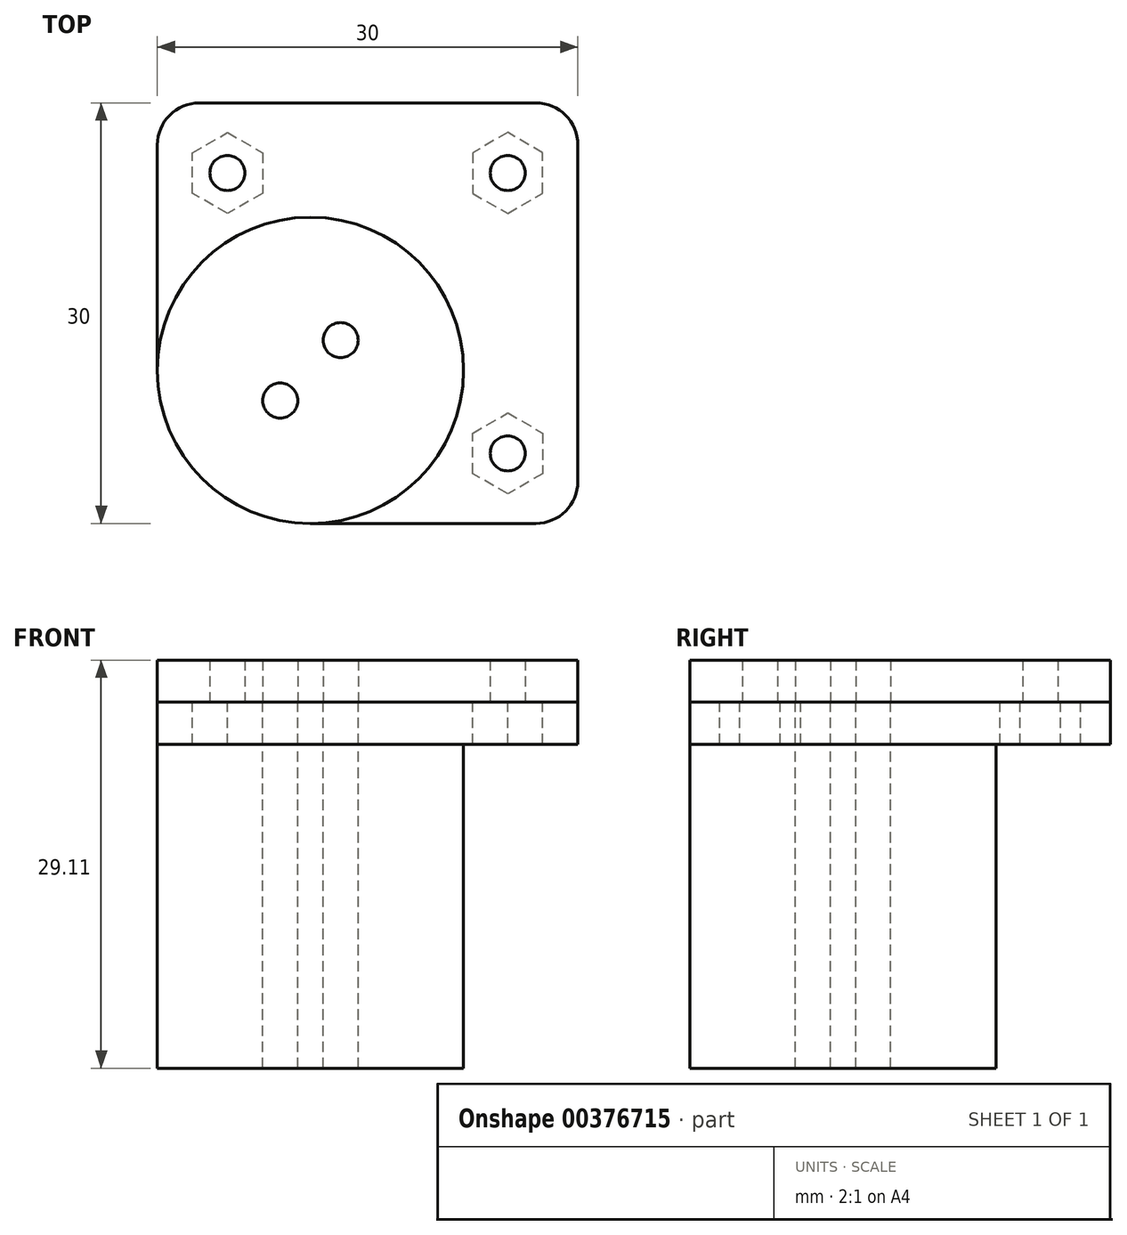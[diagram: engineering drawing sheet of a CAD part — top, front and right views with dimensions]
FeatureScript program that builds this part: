
annotation { "Feature Type Name" : "Feature", "Feature Type Description" : "" }
export const myFeature = defineFeature(function(context is Context, id is Id, definition is map)
    precondition{}
    {
        {
            var Q0;
            Q0=qCreatedBy(makeId("Top.planeOp"),FACE);
            var sketch = newSketch(context, id + "F0", { "sketchPlane" : qUnion([Q0])});
            skCircle(sketch, "E0", {"center": v(0, 0) * mm, "radius": 10.92 * mm});
            skSolve(sketch);
        }
        {
            var Q0;
            Q0 = qSketchRegion(id + "F0", true);
            extrude(context, id + "F1", {"entities" : qUnion([Q0]), "depth" : 23.1 * mm});
        }
        {
            var Q0;
            Q0=makeQuery(id+"F1.opExtrude","CAP_FACE",FACE,{"disambiguationData":[OSD([sQuery(id+"F0.wireOp",EDGE,"E0")])],"isStart":false});
            var sketch = newSketch(context, id + "F2", { "sketchPlane" : qUnion([Q0])});
            skArc(sketch, "E1", {"start": v(-10.92, 0) * mm, "mid": v(-7.72, -7.72) * mm, "end": v(0, -10.92) * mm});
            skLineSegment(sketch, "E2", {"start": v(0, 0) * mm, "end": v(0, -10.92) * mm, "construction": true});
            skLineSegment(sketch, "E3", {"start": v(0, 0) * mm, "end": v(-10.92, 0) * mm, "construction": true});
            skLineSegment(sketch, "E4", {"start": v(0, -10.92) * mm, "end": v(19.08, -10.92) * mm});
            skLineSegment(sketch, "E5", {"start": v(19.08, -10.92) * mm, "end": v(19.08, 19.08) * mm});
            skLineSegment(sketch, "E6", {"start": v(19.08, 19.08) * mm, "end": v(-10.92, 19.08) * mm});
            skLineSegment(sketch, "E7", {"start": v(-10.92, 19.08) * mm, "end": v(-10.92, 0) * mm});
            skSolve(sketch);
        }
        {
            var Q0;
            Q0 = qSketchRegion(id + "F2", true);
            extrude(context, id + "F3", {"entities" : qUnion([Q0]), "depth" : 3 * mm});
        }
        {
            var Q0;
            Q0=makeQuery(id+"F3.opExtrude","SWEPT_EDGE",EDGE,{"disambiguationData":[OSD([sQuery(id+"F2.wireOp",EDGE,"E4"),sQuery(id+"F2.wireOp",EDGE,"E5")])]});
            var Q1;
            Q1=makeQuery(id+"F3.opExtrude","SWEPT_EDGE",EDGE,{"disambiguationData":[OSD([sQuery(id+"F2.wireOp",EDGE,"E5"),sQuery(id+"F2.wireOp",EDGE,"E6")])]});
            var Q2;
            Q2=makeQuery(id+"F3.opExtrude","SWEPT_EDGE",EDGE,{"disambiguationData":[OSD([sQuery(id+"F2.wireOp",EDGE,"E6"),sQuery(id+"F2.wireOp",EDGE,"E7")])]});
            fillet(context, id + "F4", {"entities" : qUnion([Q0, Q1, Q2]), "radius" : 3 * mm, "tangentPropagation" : true, "allowEdgeOverflow" : false});
        }
        {
            var Q0;
            Q0=makeQuery(id+"F3.opExtrude","CAP_FACE",FACE,{"disambiguationData":[OSD([sQuery(id+"F2.wireOp",EDGE,"E1"),sQuery(id+"F2.wireOp",EDGE,"E4"),sQuery(id+"F2.wireOp",EDGE,"E5"),sQuery(id+"F2.wireOp",EDGE,"E6"),sQuery(id+"F2.wireOp",EDGE,"E7")])],"isStart":false});
            var sketch = newSketch(context, id + "F5", { "sketchPlane" : qUnion([Q0])});
            skLineSegment(sketch, "E8", {"start": v(-10.92, 0) * mm, "end": v(19.08, 0) * mm, "construction": true});
            skLineSegment(sketch, "E9", {"start": v(0, -10.92) * mm, "end": v(0, 19.08) * mm, "construction": true});
            skLineSegment(sketch, "E10", {"start": v(-7.72, -7.72) * mm, "end": v(0, 0) * mm, "construction": true});
            skLineSegment(sketch, "E11", {"start": v(-10.92, 10.92) * mm, "end": v(10.92, -10.92) * mm, "construction": true});
            skPoint(sketch, "E12", {"position": v(-2.16, -2.16) * mm});
            skPoint(sketch, "E13.MirrorP", {"position": v(2.16, 2.16) * mm});
            skSolve(sketch);
        }
        {
            var Q0;
            Q0=sQuery(id+"F5.wireOp",VERTEX,"E12");
            var Q1;
            Q1=sQuery(id+"F5.wireOp",VERTEX,"E13.MirrorP");
            var Q2;
            Q2=makeQuery(id+"F3.opExtrude","SWEPT_BODY",BODY,{"disambiguationData":[OSD([sQuery(id+"F2.wireOp",EDGE,"E1"),sQuery(id+"F2.wireOp",EDGE,"E4"),sQuery(id+"F2.wireOp",EDGE,"E5"),sQuery(id+"F2.wireOp",EDGE,"E6"),sQuery(id+"F2.wireOp",EDGE,"E7")])]});
            var Q3;
            Q3=makeQuery(id+"F1.opExtrude","SWEPT_BODY",BODY,{"disambiguationData":[OSD([sQuery(id+"F0.wireOp",EDGE,"E0")])]});
            hole(context, id + "F6", {"style" : HoleStyle.SIMPLE, "endStyle" : HoleEndStyle.THROUGH, "holeDiameter" : 2.5 * mm, "isTappedThrough" : true, "tappedDepth" : 12 * mm, "tapClearance" : 3, "locations" : qUnion([Q0, Q1]), "scope" : qUnion([Q2, Q3])});
        }
        {
            var Q0;
            Q0=makeQuery(id+"F3.opExtrude","CAP_FACE",FACE,{"disambiguationData":[OSD([sQuery(id+"F2.wireOp",EDGE,"E1"),sQuery(id+"F2.wireOp",EDGE,"E4"),sQuery(id+"F2.wireOp",EDGE,"E5"),sQuery(id+"F2.wireOp",EDGE,"E6"),sQuery(id+"F2.wireOp",EDGE,"E7")])],"isStart":false});
            extrude(context, id + "F7", {"entities" : qUnion([Q0]), "depth" : 3 * mm});
        }
        {
            var Q0;
            Q0=makeQuery(id+"F3.opExtrude","CAP_FACE",FACE,{"disambiguationData":[OSD([sQuery(id+"F2.wireOp",EDGE,"E1"),sQuery(id+"F2.wireOp",EDGE,"E4"),sQuery(id+"F2.wireOp",EDGE,"E5"),sQuery(id+"F2.wireOp",EDGE,"E6"),sQuery(id+"F2.wireOp",EDGE,"E7")])],"isStart":false});
            var sketch = newSketch(context, id + "F8", { "sketchPlane" : qUnion([Q0])});
            skLineSegment(sketch, "E14", {"start": v(19.08, 4.08) * mm, "end": v(-10.92, 4.08) * mm, "construction": true});
            skLineSegment(sketch, "E15", {"start": v(4.08, 19.08) * mm, "end": v(4.08, -10.92) * mm, "construction": true});
            skPoint(sketch, "E15.endSnap0", {"position": v(4.08, 4.08) * mm});
            skPoint(sketch, "E16", {"position": v(-5.92, 14.08) * mm});
            skPoint(sketch, "E17.MirrorP", {"position": v(14.08, 14.08) * mm});
            skPoint(sketch, "E18.MirrorP", {"position": v(14.08, -5.92) * mm});
            skCircle(sketch, "E19.cCircle", {"center": v(-5.92, 14.08) * mm, "radius": 2.5 * mm, "construction": true});
            skLineSegment(sketch, "E19.0", {"start": v(-3.42, 15.52) * mm, "end": v(-3.42, 12.63) * mm});
            skLineSegment(sketch, "E19.1", {"start": v(-3.42, 12.63) * mm, "end": v(-5.92, 11.2) * mm});
            skLineSegment(sketch, "E19.2", {"start": v(-5.92, 11.2) * mm, "end": v(-8.42, 12.63) * mm});
            skLineSegment(sketch, "E19.3", {"start": v(-8.42, 12.63) * mm, "end": v(-8.42, 15.52) * mm});
            skLineSegment(sketch, "E19.4", {"start": v(-8.42, 15.52) * mm, "end": v(-5.92, 16.96) * mm});
            skLineSegment(sketch, "E19.5", {"start": v(-5.92, 16.96) * mm, "end": v(-3.42, 15.52) * mm});
            skPoint(sketch, "E19.0.midPoint", {"position": v(-3.42, 14.08) * mm});
            skLineSegment(sketch, "E20.MirrorCS", {"start": v(11.58, 15.52) * mm, "end": v(11.58, 12.63) * mm});
            skLineSegment(sketch, "E21.MirrorCS", {"start": v(16.58, 15.52) * mm, "end": v(14.08, 16.96) * mm});
            skLineSegment(sketch, "E22.MirrorCS", {"start": v(11.58, 12.63) * mm, "end": v(14.08, 11.2) * mm});
            skLineSegment(sketch, "E23.MirrorCS", {"start": v(16.58, 12.63) * mm, "end": v(16.58, 15.52) * mm});
            skLineSegment(sketch, "E24.MirrorCS", {"start": v(14.08, 16.96) * mm, "end": v(11.58, 15.52) * mm});
            skCircle(sketch, "E25.MirrorC", {"center": v(14.08, 14.08) * mm, "radius": 2.5 * mm, "construction": true});
            skLineSegment(sketch, "E26.MirrorCS", {"start": v(14.08, 11.2) * mm, "end": v(16.58, 12.63) * mm});
            skPoint(sketch, "E27.MirrorP", {"position": v(11.58, 14.08) * mm});
            skLineSegment(sketch, "E28.MirrorCS", {"start": v(11.58, -7.37) * mm, "end": v(11.58, -4.48) * mm});
            skLineSegment(sketch, "E29.MirrorCS", {"start": v(14.08, -3.04) * mm, "end": v(16.58, -4.48) * mm});
            skCircle(sketch, "E30.MirrorC", {"center": v(14.08, -5.92) * mm, "radius": 2.5 * mm, "construction": true});
            skLineSegment(sketch, "E31.MirrorCS", {"start": v(14.08, -8.8) * mm, "end": v(11.58, -7.37) * mm});
            skLineSegment(sketch, "E32.MirrorCS", {"start": v(16.58, -4.48) * mm, "end": v(16.58, -7.37) * mm});
            skLineSegment(sketch, "E33.MirrorCS", {"start": v(16.58, -7.37) * mm, "end": v(14.08, -8.8) * mm});
            skLineSegment(sketch, "E34.MirrorCS", {"start": v(11.58, -4.48) * mm, "end": v(14.08, -3.04) * mm});
            skPoint(sketch, "E35.MirrorP", {"position": v(11.58, -5.92) * mm});
            skSolve(sketch);
        }
        {
            var Q0;
            Q0 = qSketchRegion(id + "F8", true);
            extrude(context, id + "F9", {"entities" : qUnion([Q0]), "operationType" : NewBodyOperationType.REMOVE, "endBound" : BoundingType.THROUGH_ALL, "oppositeDirection" : true, "depth" : 25 * mm});
        }
        {
            var Q0;
            Q0=sQuery(id+"F8.wireOp",VERTEX,"E16");
            var Q1;
            Q1=sQuery(id+"F8.wireOp",VERTEX,"E17.MirrorP");
            var Q2;
            Q2=sQuery(id+"F8.wireOp",VERTEX,"E18.MirrorP");
            var Q3;
            Q3=makeQuery(id+"F7.opExtrude","SWEPT_BODY",BODY,{"disambiguationData":[OSD([sQuery(id+"F2.wireOp",EDGE,"E1"),sQuery(id+"F2.wireOp",EDGE,"E4"),sQuery(id+"F2.wireOp",EDGE,"E5"),sQuery(id+"F2.wireOp",EDGE,"E6"),sQuery(id+"F2.wireOp",EDGE,"E7")])]});
            hole(context, id + "F10", {"style" : HoleStyle.SIMPLE, "endStyle" : HoleEndStyle.THROUGH, "oppositeDirection" : true, "holeDiameter" : 2.5 * mm, "isTappedThrough" : true, "tappedDepth" : 12 * mm, "tapClearance" : 3, "locations" : qUnion([Q0, Q1, Q2]), "scope" : qUnion([Q3])});
        }
    });
